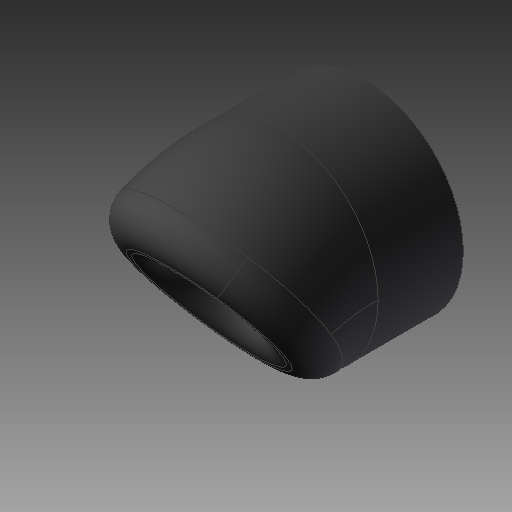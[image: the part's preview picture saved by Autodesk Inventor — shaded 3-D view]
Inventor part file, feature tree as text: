
AUTODESK INVENTOR PART (.ipt)
format: ipt  version: 2018 (Build 220112000, 112)  size: 302,592 bytes
history: native  units: mm
features: sketch x5, extrude x3, other x3, reference x2, sweep x1, fillet x1
ambient origin geometry x8: Origin, YZ Plane, XZ Plane, XY Plane, X Axis, Y Axis, Z Axis, Center Point
bodies: Solid1 (feature_tree)
feature tree (15):
  extrude  "Extrusion1"  Depth=1.0mm TaperAngle=0.0deg
  extrude  "Extrusion2"  Depth=100.0mm TaperAngle=0.0deg
  sketch  "Sketch3"  dims[d20=5.3mm d21=0.0mm d22=0.0mm]
  sketch  "Sketch4"  dims[d23=2.0mm]
  extrude  "Extrusion3"  TaperAngle=0.0deg  [1 undecoded]
  sweep  "Sweep6"
  fillet  "Fillet2"  [1 undecoded]
  sketch  "Sketch1"  dims[d0=6.0mm d1=0.0mm d2=1.0mm d3=0.0mm]
  reference  "Reference1"
  reference  "Reference2"
  sketch  "Sketch2"  dims[d17=5.3mm d18=100.0mm d19=0.0mm]
  sketch  "Sketch8"
  other  "<userpath>\OneDrive\Documents\Inventor\TSA\2018\Animatronics\Tortoise\TurtleAssembly2.iam"
  other  "TurtleAssembly2.iam"
  other  "Face:1"
note: 2 required parameter values undecoded (feature->parameter linkage not recoverable at this tier; creation-order binding heuristic only, values carry confidence <= 0.55)
